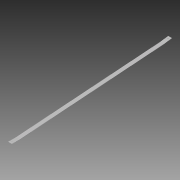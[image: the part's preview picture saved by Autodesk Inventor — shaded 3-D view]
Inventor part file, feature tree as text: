
AUTODESK INVENTOR PART (.ipt)
format: ipt  version: 2014 (Build 180170000, 170)  size: 167,424 bytes
history: native  units: in
note: dims shown in document units (in); Inventor stores cm internally (conversion verified against a paired STEP export)
features: sketch x6, hole x3, sheet_metal_op x2, extrude x1, other x1
ambient origin geometry x8: Origin, YZ Plane, XZ Plane, XY Plane, X Axis, Y Axis, Z Axis, Center Point
bodies: Solid1 (feature_tree)
feature tree (13):
  extrude  "Extrusion1"  Depth=0.0394in
  hole  "Hole1"  [1 undecoded]
  hole  "Hole2"  [1 undecoded]
  sheet_metal_op  "Fold1"
  sheet_metal_op  "Fold2"
  hole  "Hole3"  [1 undecoded]
  sketch  "Sketch1"  dims[d0=1.5in d1=0.0394in]
  sketch  "Sketch2"  dims[d2=63.937in d3=0.0in d4=0.7874in]
  sketch  "Sketch3"  dims[d5=0.1969in d6=0.75in d7=0.375in d8=0.25in d9=0.5635in d10=1.0in d11=0.8108in d12=0.7874in]
  sketch  "Sketch4"  dims[d13=0.1969in d14=0.75in d15=0.375in d16=0.25in d17=0.5635in d18=1.0in d19=0.8108in d20=2.3622in]
  sketch  "Sketch5"  dims[d21=0.0in]
  sketch  "Sketch6"  dims[d22=0.0394in d23=0.0197in d24=0.0787in d25=0.0394in d26=0.0285in d27=0.0394in d28=2.3622in d29=0.0in d30=0.0394in d31=0.0197in d32=0.0787in d33=0.0394in d34=0.0285in d35=0.0394in d36=7.874in d37=0.0394in d38=0.2362in d39=0.1575in d40=0.0787in d41=90.0deg d42=0.0394in d43=0.8108in]
  other  "Definition1"
note: 3 required parameter values undecoded (feature->parameter linkage not recoverable at this tier; creation-order binding heuristic only, values carry confidence <= 0.55)
